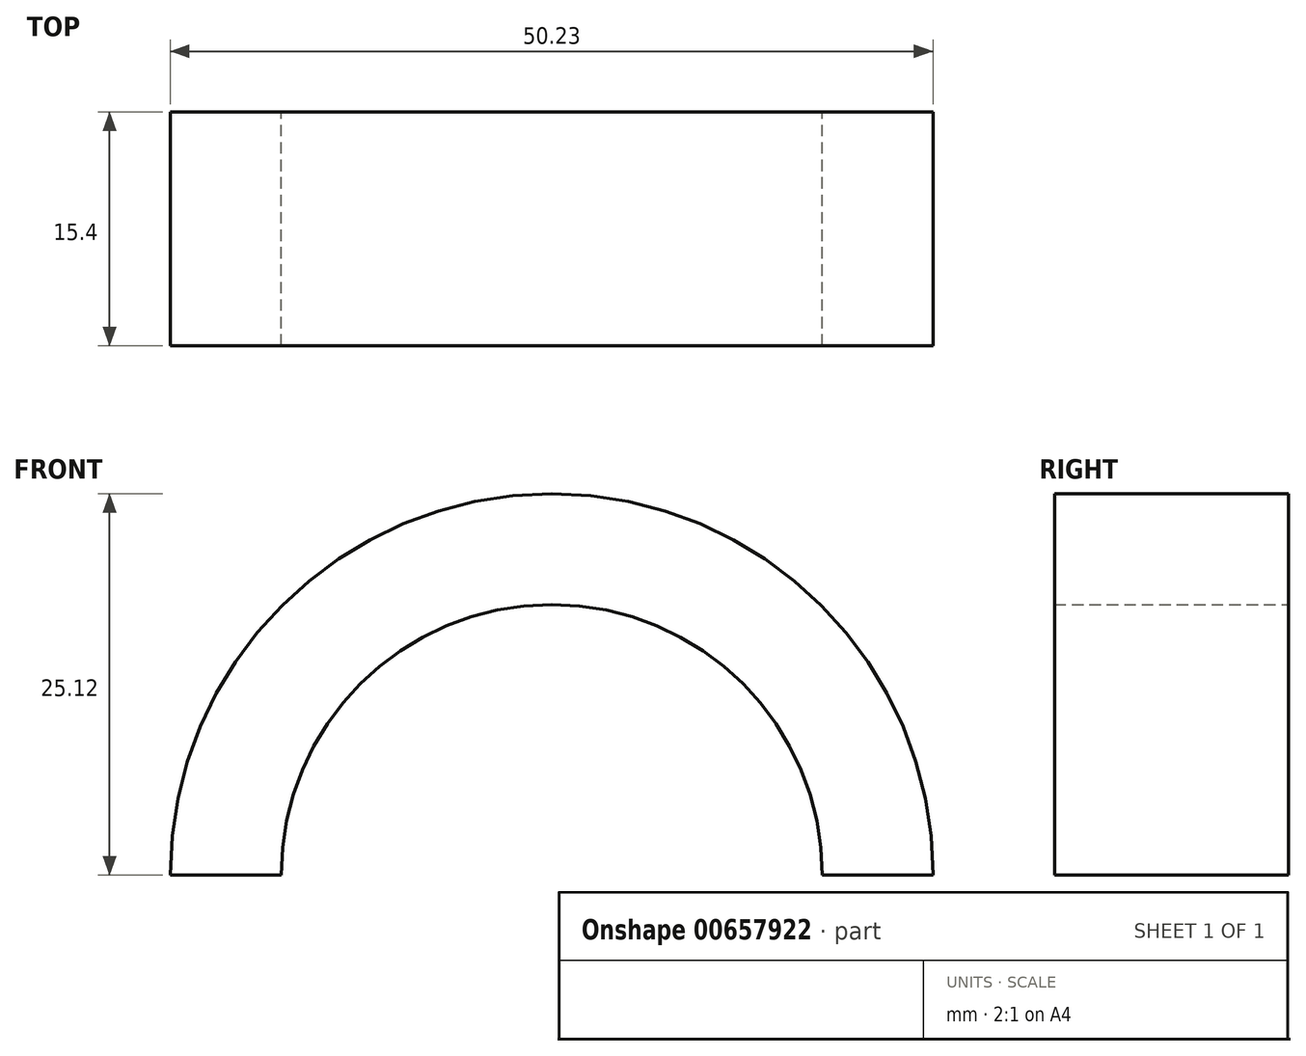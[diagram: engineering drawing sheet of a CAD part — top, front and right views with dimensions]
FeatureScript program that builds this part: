
annotation { "Feature Type Name" : "Feature", "Feature Type Description" : "" }
export const myFeature = defineFeature(function(context is Context, id is Id, definition is map)
    precondition{}
    {
        {
            var Q0;
            Q0=qCreatedBy(makeId("Front.planeOp"),FACE);
            var sketch = newSketch(context, id + "F0", { "sketchPlane" : qUnion([Q0])});
            skArc(sketch, "E0", {"start": v(-4.42, 16.74) * mm, "mid": v(-29.53, 41.86) * mm, "end": v(-54.65, 16.74) * mm});
            skArc(sketch, "E1.0", {"start": v(-11.72, 16.74) * mm, "mid": v(-29.53, 34.56) * mm, "end": v(-47.35, 16.74) * mm});
            skLineSegment(sketch, "E2", {"start": v(-54.65, 16.74) * mm, "end": v(-47.35, 16.74) * mm});
            skLineSegment(sketch, "E3", {"start": v(-11.72, 16.74) * mm, "end": v(-4.42, 16.74) * mm});
            skSolve(sketch);
        }
        {
            var Q0;
            Q0 = qSketchRegion(id + "F0", true);
            extrude(context, id + "F1", {"entities" : qUnion([Q0]), "depth" : 15.4 * mm, "offsetDistance" : 25 * mm});
        }
    });
